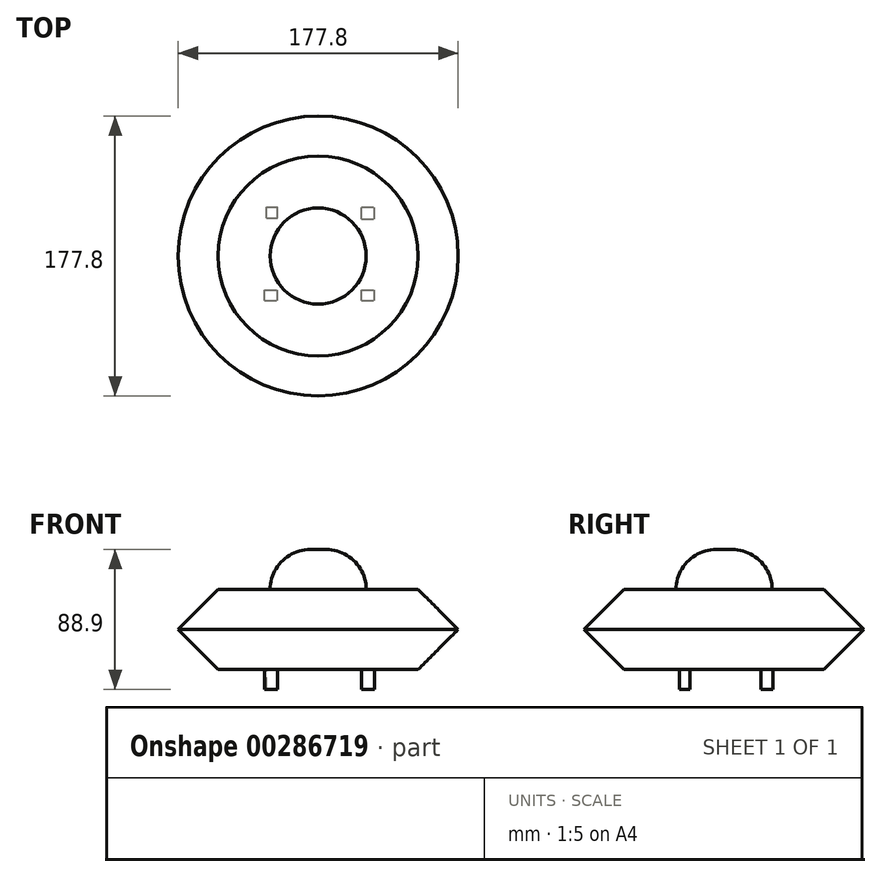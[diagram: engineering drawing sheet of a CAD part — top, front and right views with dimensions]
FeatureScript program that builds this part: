
annotation { "Feature Type Name" : "Feature", "Feature Type Description" : "" }
export const myFeature = defineFeature(function(context is Context, id is Id, definition is map)
    precondition{}
    {
        {
            var Q0;
            Q0=qCreatedBy(makeId("Top.planeOp"),FACE);
            var sketch = newSketch(context, id + "F0", { "sketchPlane" : qUnion([Q0])});
            skCircle(sketch, "E0", {"center": v(0, 0) * mm, "radius": 88.9 * mm});
            skSolve(sketch);
        }
        {
            var Q0;
            Q0=makeQuery(id+"F0.imprint","IMPRINT",FACE,{"disambiguationData":[TD([[makeQuery(id+"F0.imprint","IMPRINT",EDGE,{"derivedFrom":sQuery(id+"F0.wireOp",EDGE,"E0")}),1.0]])]});
            extrude(context, id + "F1", {"entities" : qUnion([Q0]), "depth" : 50.8 * mm});
        }
        {
            var Q0;
            Q0=makeQuery(id+"F1.opExtrude","CAP_FACE",FACE,{"disambiguationData":[OSD([sQuery(id+"F0.wireOp",EDGE,"E0")])],"isStart":false});
            chamfer(context, id + "F2", {"entities" : qUnion([Q0]), "width" : 25.4 * mm, "tangentPropagation" : true});
        }
        {
            var Q0;
            Q0=makeQuery(id+"F1.opExtrude","CAP_FACE",FACE,{"disambiguationData":[OSD([sQuery(id+"F0.wireOp",EDGE,"E0")])],"isStart":true});
            chamfer(context, id + "F3", {"entities" : qUnion([Q0]), "width" : 25.4 * mm, "tangentPropagation" : true});
        }
        {
            var Q0;
            Q0=makeQuery(id+"F1.opExtrude","CAP_FACE",FACE,{"disambiguationData":[OSD([sQuery(id+"F0.wireOp",EDGE,"E0")])],"isStart":false});
            var sketch = newSketch(context, id + "F4", { "sketchPlane" : qUnion([Q0])});
            skCircle(sketch, "E1", {"center": v(0, 0) * mm, "radius": 30.49 * mm});
            skSolve(sketch);
        }
        {
            var Q0;
            Q0=makeQuery(id+"F4.imprint","IMPRINT",FACE,{"disambiguationData":[TD([[makeQuery(id+"F4.imprint","IMPRINT",EDGE,{"derivedFrom":sQuery(id+"F4.wireOp",EDGE,"E1")}),1.0]])]});
            extrude(context, id + "F5", {"entities" : qUnion([Q0]), "operationType" : NewBodyOperationType.ADD, "depth" : 25.4 * mm});
        }
        {
            var Q0;
            Q0=makeQuery(id+"F5.opExtrude","CAP_FACE",FACE,{"disambiguationData":[OSD([sQuery(id+"F4.wireOp",EDGE,"E1")])],"isStart":false});
            fillet(context, id + "F6", {"entities" : qUnion([Q0]), "radius" : 25.4 * mm, "tangentPropagation" : true, "allowEdgeOverflow" : false});
        }
        {
            var Q0;
            Q0=makeQuery(id+"F1.opExtrude","CAP_FACE",FACE,{"disambiguationData":[OSD([sQuery(id+"F0.wireOp",EDGE,"E0")])],"isStart":true});
            var sketch = newSketch(context, id + "F7", { "sketchPlane" : qUnion([Q0])});
            skLineSegment(sketch, "E2.bottom", {"start": v(-33.91, 28.28) * mm, "end": v(-25.85, 28.28) * mm});
            skLineSegment(sketch, "E2.top", {"start": v(-33.91, 21.56) * mm, "end": v(-25.85, 21.56) * mm});
            skLineSegment(sketch, "E2.left", {"start": v(-33.91, 28.28) * mm, "end": v(-33.91, 21.56) * mm});
            skLineSegment(sketch, "E2.right", {"start": v(-25.85, 28.28) * mm, "end": v(-25.85, 21.56) * mm});
            skLineSegment(sketch, "E3.bottom", {"start": v(-32.9, -24.1) * mm, "end": v(-25.85, -24.1) * mm});
            skLineSegment(sketch, "E3.top", {"start": v(-32.9, -31.16) * mm, "end": v(-25.85, -31.16) * mm});
            skLineSegment(sketch, "E3.left", {"start": v(-32.9, -24.1) * mm, "end": v(-32.9, -31.16) * mm});
            skLineSegment(sketch, "E3.right", {"start": v(-25.85, -24.1) * mm, "end": v(-25.85, -31.16) * mm});
            skLineSegment(sketch, "E4.bottom", {"start": v(27.53, 28.28) * mm, "end": v(35.93, 28.28) * mm});
            skLineSegment(sketch, "E4.top", {"start": v(27.53, 21.56) * mm, "end": v(35.93, 21.56) * mm});
            skLineSegment(sketch, "E4.left", {"start": v(27.53, 28.28) * mm, "end": v(27.53, 21.56) * mm});
            skLineSegment(sketch, "E4.right", {"start": v(35.93, 28.28) * mm, "end": v(35.93, 21.56) * mm});
            skPoint(sketch, "E5.firstSnap0", {"position": v(27.53, 24.92) * mm});
            skLineSegment(sketch, "E5.bottom", {"start": v(27.53, -23.43) * mm, "end": v(35.93, -23.43) * mm});
            skLineSegment(sketch, "E5.top", {"start": v(27.53, -31.16) * mm, "end": v(35.93, -31.16) * mm});
            skLineSegment(sketch, "E5.left", {"start": v(27.53, -23.43) * mm, "end": v(27.53, -31.16) * mm});
            skLineSegment(sketch, "E5.right", {"start": v(35.93, -23.43) * mm, "end": v(35.93, -31.16) * mm});
            skSolve(sketch);
        }
        {
            var Q0;
            Q0=makeQuery(id+"F7.imprint","IMPRINT",FACE,{"disambiguationData":[TD([[makeQuery(id+"F7.imprint","IMPRINT",EDGE,{"derivedFrom":sQuery(id+"F7.wireOp",EDGE,"E4.bottom")}),-1.0]])]});
            var Q1;
            Q1=makeQuery(id+"F7.imprint","IMPRINT",FACE,{"disambiguationData":[TD([[makeQuery(id+"F7.imprint","IMPRINT",EDGE,{"derivedFrom":sQuery(id+"F7.wireOp",EDGE,"E2.bottom")}),-1.0]])]});
            var Q2;
            Q2=makeQuery(id+"F7.imprint","IMPRINT",FACE,{"disambiguationData":[TD([[makeQuery(id+"F7.imprint","IMPRINT",EDGE,{"derivedFrom":sQuery(id+"F7.wireOp",EDGE,"E3.bottom")}),-1.0]])]});
            var Q3;
            Q3=makeQuery(id+"F7.imprint","IMPRINT",FACE,{"disambiguationData":[TD([[makeQuery(id+"F7.imprint","IMPRINT",EDGE,{"derivedFrom":sQuery(id+"F7.wireOp",EDGE,"E5.bottom")}),-1.0]])]});
            extrude(context, id + "F8", {"entities" : qUnion([Q0, Q1, Q2, Q3]), "operationType" : NewBodyOperationType.ADD, "depth" : 12.7 * mm});
        }
    });
